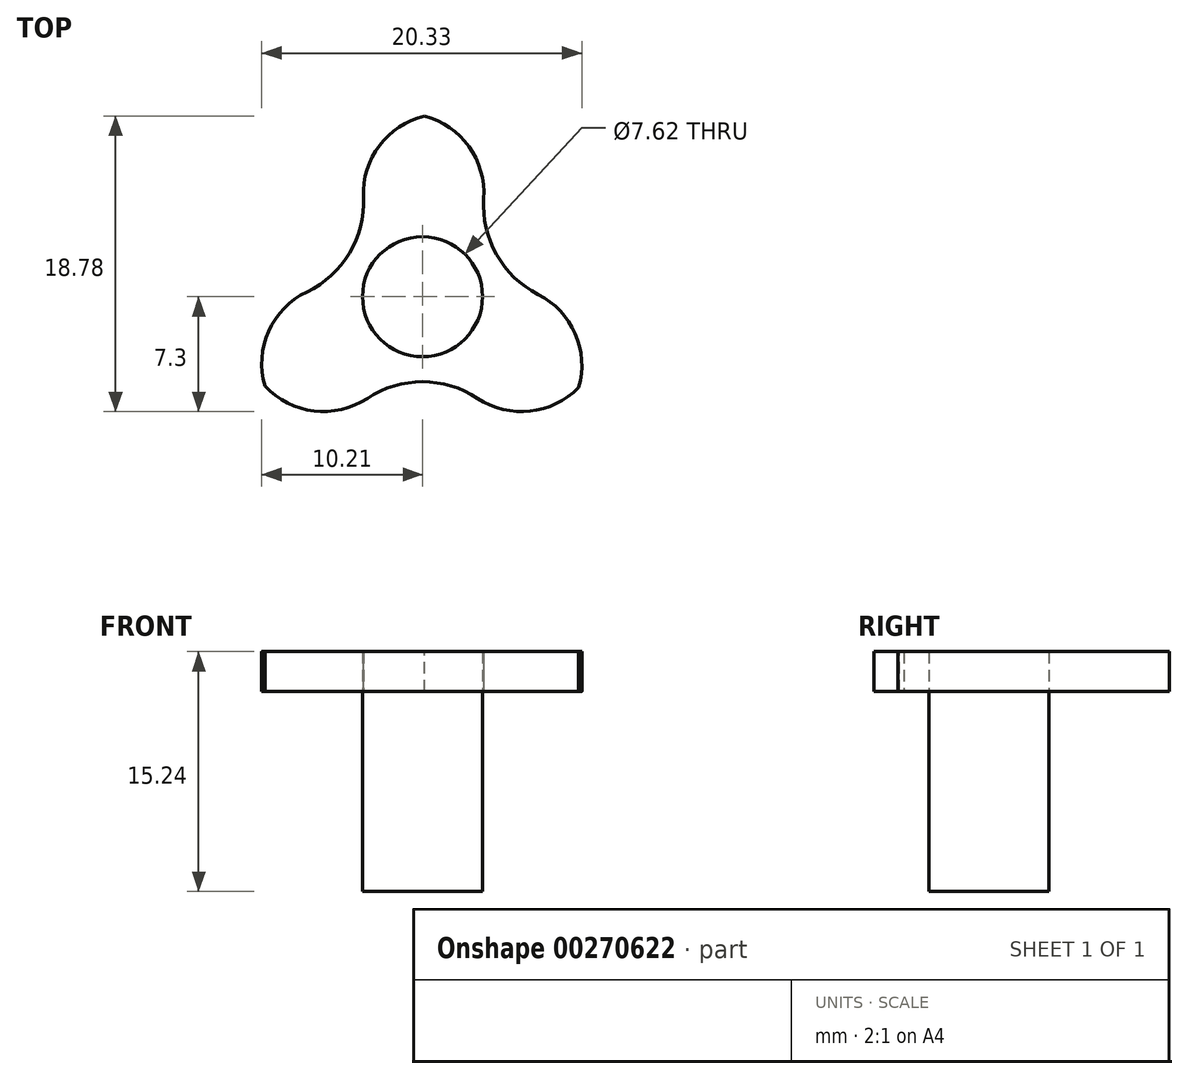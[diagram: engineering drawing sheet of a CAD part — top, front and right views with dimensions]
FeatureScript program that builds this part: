
annotation { "Feature Type Name" : "Feature", "Feature Type Description" : "" }
export const myFeature = defineFeature(function(context is Context, id is Id, definition is map)
    precondition{}
    {
        {
            var Q0;
            Q0=qCreatedBy(makeId("Top.planeOp"),FACE);
            var sketch = newSketch(context, id + "F0", { "sketchPlane" : qUnion([Q0])});
            skCircle(sketch, "E0", {"center": v(0, 0) * mm, "radius": 3.8 * mm});
            skSolve(sketch);
        }
        {
            var Q0;
            Q0=makeQuery(id+"F0.imprint","IMPRINT",FACE,{"disambiguationData":[TD([[makeQuery(id+"F0.imprint","IMPRINT",EDGE,{"derivedFrom":sQuery(id+"F0.wireOp",EDGE,"E0")}),1.0]])]});
            extrude(context, id + "F1", {"entities" : qUnion([Q0]), "depth" : 12.7 * mm});
        }
        {
            var Q0;
            Q0=makeQuery(id+"F1.opExtrude","CAP_FACE",FACE,{"disambiguationData":[OSD([sQuery(id+"F0.wireOp",EDGE,"E0")])],"isStart":false});
            var sketch = newSketch(context, id + "F2", { "sketchPlane" : qUnion([Q0])});
            skCircle(sketch, "E1", {"center": v(0, 0) * mm, "radius": 11.76 * mm});
            skCircle(sketch, "E2", {"center": v(-10.1, 6.02) * mm, "radius": 6.35 * mm});
            skCircle(sketch, "E3", {"center": v(10.22, 5.8) * mm, "radius": 6.35 * mm});
            skCircle(sketch, "E4", {"center": v(0, -11.76) * mm, "radius": 6.35 * mm});
            skSolve(sketch);
        }
        {
            var Q0;
            Q0=makeQuery(id+"F2.imprint","IMPRINT",FACE,{"disambiguationData":[TD([[makeQuery(id+"F2.imprint","IMPRINT",EDGE,{"derivedFrom":makeQuery(id+"F1.opExtrude","CAP_EDGE",EDGE,{"disambiguationData":[OSD([sQuery(id+"F0.wireOp",EDGE,"E0")])],"isStart":false})}),-1.0]])]});
            extrude(context, id + "F3", {"entities" : qUnion([Q0]), "depth" : 2.54 * mm});
        }
        {
            var Q0;
            {var subQ0=sQuery(id+"F2.wireOp",EDGE,"E3");var subQ1=sQuery(id+"F2.wireOp",EDGE,"E1");Q0=makeQuery(id+"F3.opExtrude","SWEPT_EDGE",EDGE,{"disambiguationData":[OSD([subQ1,subQ0]),TDD([makeQuery(id+"F2.imprint","INTERSECT",VERTEX,{"disambiguationData":[OD(1.0)],"derivedFrom":[subQ1,subQ0]})])]});}
            var Q1;
            {var subQ0=sQuery(id+"F2.wireOp",EDGE,"E3");var subQ1=sQuery(id+"F2.wireOp",EDGE,"E1");Q1=makeQuery(id+"F3.opExtrude","SWEPT_EDGE",EDGE,{"disambiguationData":[OSD([subQ1,subQ0]),TDD([makeQuery(id+"F2.imprint","INTERSECT",VERTEX,{"disambiguationData":[OD(0.0)],"derivedFrom":[subQ1,subQ0]})])]});}
            var Q2;
            {var subQ0=sQuery(id+"F2.wireOp",EDGE,"E2");var subQ1=sQuery(id+"F2.wireOp",EDGE,"E1");Q2=makeQuery(id+"F3.opExtrude","SWEPT_EDGE",EDGE,{"disambiguationData":[OSD([subQ1,subQ0]),TDD([makeQuery(id+"F2.imprint","INTERSECT",VERTEX,{"disambiguationData":[OD(0.0)],"derivedFrom":[subQ1,subQ0]})])]});}
            var Q3;
            {var subQ0=sQuery(id+"F2.wireOp",EDGE,"E2");var subQ1=sQuery(id+"F2.wireOp",EDGE,"E1");Q3=makeQuery(id+"F3.opExtrude","SWEPT_EDGE",EDGE,{"disambiguationData":[OSD([subQ1,subQ0]),TDD([makeQuery(id+"F2.imprint","INTERSECT",VERTEX,{"disambiguationData":[OD(1.0)],"derivedFrom":[subQ1,subQ0]})])]});}
            var Q4;
            {var subQ0=sQuery(id+"F2.wireOp",EDGE,"E4");var subQ1=sQuery(id+"F2.wireOp",EDGE,"E1");Q4=makeQuery(id+"F3.opExtrude","SWEPT_EDGE",EDGE,{"disambiguationData":[OSD([subQ1,subQ0]),TDD([makeQuery(id+"F2.imprint","INTERSECT",VERTEX,{"disambiguationData":[OD(0.0)],"derivedFrom":[subQ1,subQ0]})])]});}
            var Q5;
            {var subQ0=sQuery(id+"F2.wireOp",EDGE,"E4");var subQ1=sQuery(id+"F2.wireOp",EDGE,"E1");Q5=makeQuery(id+"F3.opExtrude","SWEPT_EDGE",EDGE,{"disambiguationData":[OSD([subQ1,subQ0]),TDD([makeQuery(id+"F2.imprint","INTERSECT",VERTEX,{"disambiguationData":[OD(1.0)],"derivedFrom":[subQ1,subQ0]})])]});}
            fillet(context, id + "F4", {"entities" : qUnion([Q0, Q1, Q2, Q3, Q4, Q5]), "radius" : 5.08 * mm, "tangentPropagation" : true, "allowEdgeOverflow" : false});
        }
    });
